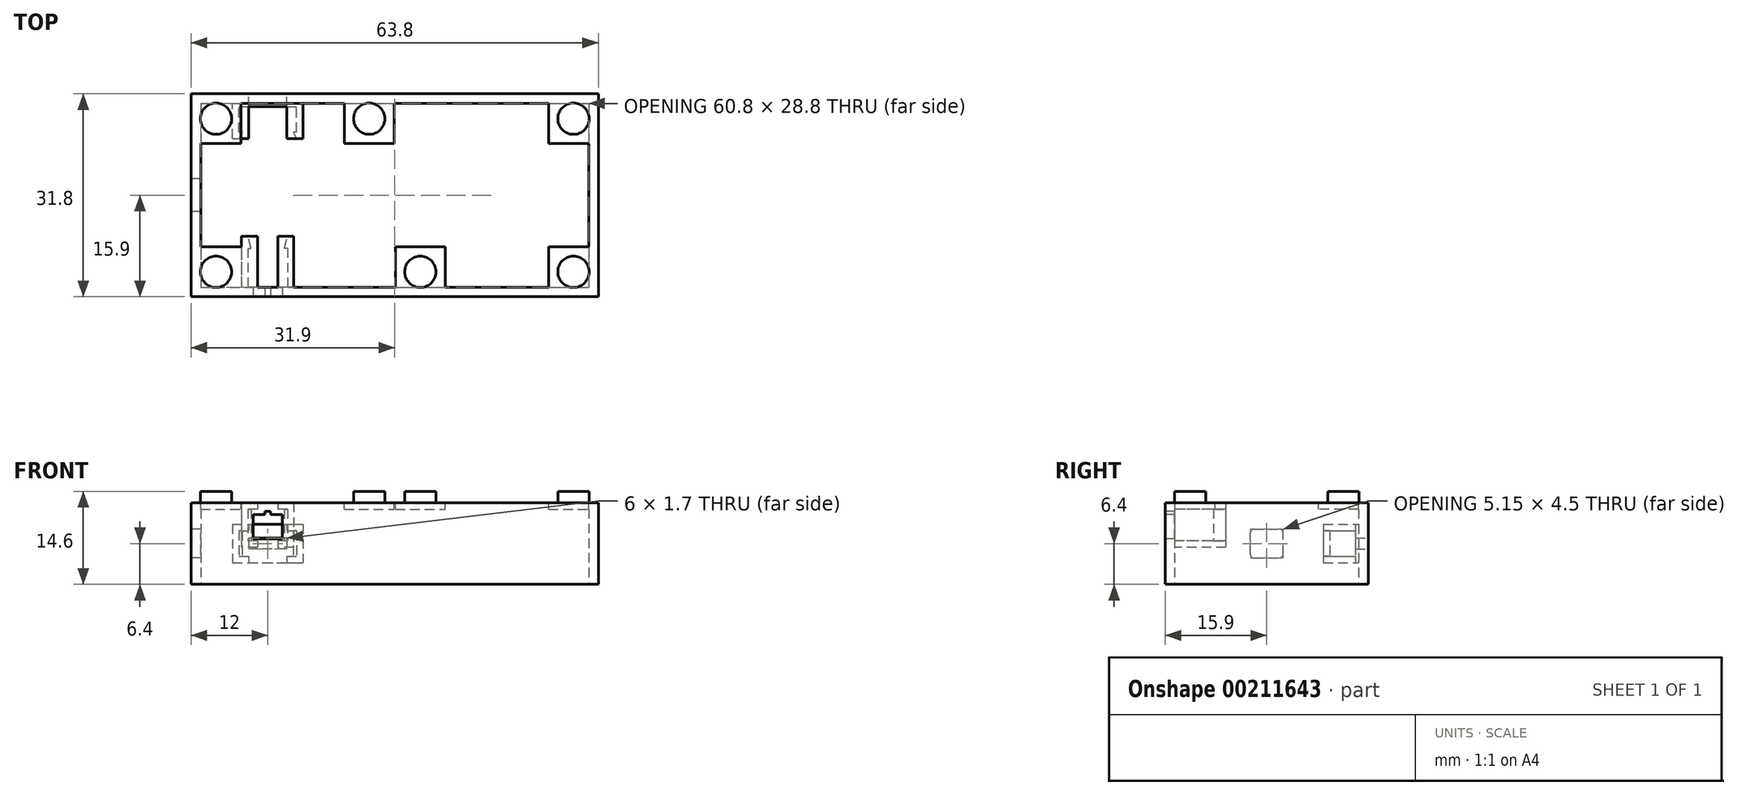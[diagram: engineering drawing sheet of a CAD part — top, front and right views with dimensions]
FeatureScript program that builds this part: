
annotation { "Feature Type Name" : "Feature", "Feature Type Description" : "" }
export const myFeature = defineFeature(function(context is Context, id is Id, definition is map)
    precondition{}
    {
        {
            var Q0;
            Q0=qCreatedBy(makeId("Top.planeOp"),FACE);
            var sketch = newSketch(context, id + "F0", { "sketchPlane" : qUnion([Q0])});
            skLineSegment(sketch, "E0.bottom", {"start": v(0, 31.8) * mm, "end": v(63.8, 31.8) * mm});
            skLineSegment(sketch, "E0.top", {"start": v(0, 0) * mm, "end": v(63.8, 0) * mm});
            skLineSegment(sketch, "E0.left", {"start": v(0, 31.8) * mm, "end": v(0, 0) * mm});
            skLineSegment(sketch, "E0.right", {"start": v(63.8, 31.8) * mm, "end": v(63.8, 0) * mm});
            skPoint(sketch, "E1", {"position": v(31.9, 31.8) * mm});
            skPoint(sketch, "E2", {"position": v(0, 15.9) * mm});
            skLineSegment(sketch, "E3.0", {"start": v(1.5, 30.3) * mm, "end": v(1.5, 1.5) * mm});
            skLineSegment(sketch, "E3.1", {"start": v(1.5, 30.3) * mm, "end": v(62.3, 30.3) * mm});
            skLineSegment(sketch, "E3.2", {"start": v(62.3, 30.3) * mm, "end": v(62.3, 1.5) * mm});
            skLineSegment(sketch, "E3.3", {"start": v(1.5, 1.5) * mm, "end": v(62.3, 1.5) * mm});
            skSolve(sketch);
        }
        {
            var Q0;
            Q0=qSketchRegion(id+"F0",true);
            extrude(context, id + "F1", {"entities" : qUnion([Q0]), "depth" : 12.8 * mm});
        }
        {
            var Q0;
            Q0=makeQuery(id+"F1.opExtrude","CAP_FACE",FACE,{"disambiguationData":[OSD([sQuery(id+"F0.wireOp",EDGE,"E0.bottom"),sQuery(id+"F0.wireOp",EDGE,"E0.top"),sQuery(id+"F0.wireOp",EDGE,"E0.left"),sQuery(id+"F0.wireOp",EDGE,"E0.right"),sQuery(id+"F0.wireOp",EDGE,"E3.0"),sQuery(id+"F0.wireOp",EDGE,"E3.1"),sQuery(id+"F0.wireOp",EDGE,"E3.2"),sQuery(id+"F0.wireOp",EDGE,"E3.3")])],"isStart":false});
            var sketch = newSketch(context, id + "F2", { "sketchPlane" : qUnion([Q0])});
            skLineSegment(sketch, "E4.bottom", {"start": v(0, 31.8) * mm, "end": v(7.8, 31.8) * mm});
            skLineSegment(sketch, "E4.top", {"start": v(0, 24) * mm, "end": v(7.8, 24) * mm});
            skLineSegment(sketch, "E4.left", {"start": v(0, 31.8) * mm, "end": v(0, 24) * mm});
            skLineSegment(sketch, "E4.right", {"start": v(7.8, 31.8) * mm, "end": v(7.8, 24) * mm});
            skLineSegment(sketch, "E5.bottom", {"start": v(0, 0) * mm, "end": v(7.8, 0) * mm});
            skLineSegment(sketch, "E5.top", {"start": v(0, 7.8) * mm, "end": v(7.8, 7.8) * mm});
            skLineSegment(sketch, "E5.left", {"start": v(0, 0) * mm, "end": v(0, 7.8) * mm});
            skLineSegment(sketch, "E5.right", {"start": v(7.8, 0) * mm, "end": v(7.8, 7.8) * mm});
            skLineSegment(sketch, "E6.bottom", {"start": v(63.8, 31.8) * mm, "end": v(56, 31.8) * mm});
            skLineSegment(sketch, "E6.top", {"start": v(63.8, 24) * mm, "end": v(56, 24) * mm});
            skLineSegment(sketch, "E6.left", {"start": v(63.8, 31.8) * mm, "end": v(63.8, 24) * mm});
            skLineSegment(sketch, "E6.right", {"start": v(56, 31.8) * mm, "end": v(56, 24) * mm});
            skLineSegment(sketch, "E7.bottom", {"start": v(63.8, 0) * mm, "end": v(56, 0) * mm});
            skLineSegment(sketch, "E7.top", {"start": v(63.8, 7.8) * mm, "end": v(56, 7.8) * mm});
            skLineSegment(sketch, "E7.left", {"start": v(63.8, 0) * mm, "end": v(63.8, 7.8) * mm});
            skLineSegment(sketch, "E7.right", {"start": v(56, 0) * mm, "end": v(56, 7.8) * mm});
            skPoint(sketch, "E8.centerSnap0", {"position": v(3.9, 24) * mm});
            skPoint(sketch, "E8.centerSnap1", {"position": v(0, 27.9) * mm});
            skPoint(sketch, "E9.centerSnap0", {"position": v(3.9, 0) * mm});
            skPoint(sketch, "E9.centerSnap1", {"position": v(0, 3.9) * mm});
            skPoint(sketch, "E10.centerSnap0", {"position": v(63.8, 27.9) * mm});
            skPoint(sketch, "E10.centerSnap1", {"position": v(59.9, 31.8) * mm});
            skPoint(sketch, "E11.centerSnap0", {"position": v(59.9, 0) * mm});
            skPoint(sketch, "E11.centerSnap1", {"position": v(63.8, 3.9) * mm});
            skLineSegment(sketch, "E12.bottom", {"start": v(24, 31.8) * mm, "end": v(31.8, 31.8) * mm});
            skLineSegment(sketch, "E12.top", {"start": v(24, 24) * mm, "end": v(31.8, 24) * mm});
            skLineSegment(sketch, "E12.left", {"start": v(24, 31.8) * mm, "end": v(24, 24) * mm});
            skLineSegment(sketch, "E12.right", {"start": v(31.8, 31.8) * mm, "end": v(31.8, 24) * mm});
            skLineSegment(sketch, "E13.bottom", {"start": v(39.8, 0) * mm, "end": v(32, 0) * mm});
            skLineSegment(sketch, "E13.top", {"start": v(39.8, 7.8) * mm, "end": v(32, 7.8) * mm});
            skLineSegment(sketch, "E13.left", {"start": v(39.8, 0) * mm, "end": v(39.8, 7.8) * mm});
            skLineSegment(sketch, "E13.right", {"start": v(32, 0) * mm, "end": v(32, 7.8) * mm});
            skPoint(sketch, "E14", {"position": v(27.9, 31.8) * mm});
            skPoint(sketch, "E15", {"position": v(35.9, 0) * mm});
            skSolve(sketch);
        }
        {
            var Q0;
            {var subQ0=sQuery(id+"F2.wireOp",EDGE,"E4.right");var subQ1=sQuery(id+"F2.wireOp",EDGE,"E4.top");var subQ2=makeQuery(id+"F2.imprint","INTERSECT",VERTEX,{"derivedFrom":[subQ1,subQ0]});Q0=makeQuery(id+"F2.imprint","IMPRINT",FACE,{"disambiguationData":[TD([[makeQuery(id+"F2.imprint","IMPRINT",EDGE,{"disambiguationData":[TD([[subQ2,1.0]])],"derivedFrom":subQ1}),1.0]])]});}
            var Q1;
            {var subQ0=sQuery(id+"F2.wireOp",EDGE,"E5.right");var subQ1=sQuery(id+"F2.wireOp",EDGE,"E5.top");var subQ2=makeQuery(id+"F2.imprint","INTERSECT",VERTEX,{"derivedFrom":[subQ1,subQ0]});Q1=makeQuery(id+"F2.imprint","IMPRINT",FACE,{"disambiguationData":[TD([[makeQuery(id+"F2.imprint","IMPRINT",EDGE,{"disambiguationData":[TD([[subQ2,1.0]])],"derivedFrom":subQ1}),-1.0]])]});}
            var Q2;
            {var subQ0=sQuery(id+"F2.wireOp",EDGE,"E7.right");var subQ1=sQuery(id+"F2.wireOp",EDGE,"E7.top");var subQ2=makeQuery(id+"F2.imprint","INTERSECT",VERTEX,{"derivedFrom":[subQ1,subQ0]});Q2=makeQuery(id+"F2.imprint","IMPRINT",FACE,{"disambiguationData":[TD([[makeQuery(id+"F2.imprint","IMPRINT",EDGE,{"disambiguationData":[TD([[subQ2,1.0]])],"derivedFrom":subQ1}),1.0]])]});}
            var Q3;
            {var subQ0=sQuery(id+"F2.wireOp",EDGE,"E6.right");var subQ1=sQuery(id+"F2.wireOp",EDGE,"E6.top");var subQ2=makeQuery(id+"F2.imprint","INTERSECT",VERTEX,{"derivedFrom":[subQ1,subQ0]});Q3=makeQuery(id+"F2.imprint","IMPRINT",FACE,{"disambiguationData":[TD([[makeQuery(id+"F2.imprint","IMPRINT",EDGE,{"disambiguationData":[TD([[subQ2,1.0]])],"derivedFrom":subQ1}),-1.0]])]});}
            var Q4;
            {var subQ0=sQuery(id+"F2.wireOp",EDGE,"E12.top");Q4=makeQuery(id+"F2.imprint","IMPRINT",FACE,{"disambiguationData":[TD([[makeQuery(id+"F2.imprint","IMPRINT",EDGE,{"derivedFrom":subQ0}),1.0]])]});}
            var Q5;
            {var subQ0=sQuery(id+"F2.wireOp",EDGE,"E13.top");Q5=makeQuery(id+"F2.imprint","IMPRINT",FACE,{"disambiguationData":[TD([[makeQuery(id+"F2.imprint","IMPRINT",EDGE,{"derivedFrom":subQ0}),1.0]])]});}
            extrude(context, id + "F3", {"entities" : qUnion([Q0, Q1, Q2, Q3, Q4, Q5]), "operationType" : NewBodyOperationType.ADD, "oppositeDirection" : true, "depth" : 1 * mm});
        }
        {
            var Q0;
            {var subQ0=sQuery(id+"F0.wireOp",EDGE,"E3.3");var subQ1=sQuery(id+"F0.wireOp",EDGE,"E3.2");var subQ2=sQuery(id+"F0.wireOp",EDGE,"E3.1");var subQ3=sQuery(id+"F0.wireOp",EDGE,"E3.0");Q0=makeQuery(id+"F3.boolean.opBoolean","MERGE",FACE,{"derivedFrom":[makeQuery(id+"F1.opExtrude","CAP_FACE",FACE,{"disambiguationData":[OSD([sQuery(id+"F0.wireOp",EDGE,"E0.bottom"),sQuery(id+"F0.wireOp",EDGE,"E0.top"),sQuery(id+"F0.wireOp",EDGE,"E0.left"),sQuery(id+"F0.wireOp",EDGE,"E0.right"),subQ3,subQ2,subQ1,subQ0])],"isStart":false}),makeQuery(id+"F3.opExtrude","CAP_FACE",FACE,{"disambiguationData":[OSD([subQ3,subQ2,sQuery(id+"F2.wireOp",EDGE,"E4.top"),sQuery(id+"F2.wireOp",EDGE,"E4.right")])],"isStart":true}),makeQuery(id+"F3.opExtrude","CAP_FACE",FACE,{"disambiguationData":[OSD([subQ3,subQ0,sQuery(id+"F2.wireOp",EDGE,"E5.top"),sQuery(id+"F2.wireOp",EDGE,"E5.right")])],"isStart":true}),makeQuery(id+"F3.opExtrude","CAP_FACE",FACE,{"disambiguationData":[OSD([subQ2,subQ1,sQuery(id+"F2.wireOp",EDGE,"E6.top"),sQuery(id+"F2.wireOp",EDGE,"E6.right")])],"isStart":true}),makeQuery(id+"F3.opExtrude","CAP_FACE",FACE,{"disambiguationData":[OSD([subQ1,subQ0,sQuery(id+"F2.wireOp",EDGE,"E7.top"),sQuery(id+"F2.wireOp",EDGE,"E7.right")])],"isStart":true})]});}
            var sketch = newSketch(context, id + "F4", { "sketchPlane" : qUnion([Q0])});
            skLineSegment(sketch, "E16.bottom", {"start": v(0, 31.8) * mm, "end": v(7.8, 31.8) * mm});
            skLineSegment(sketch, "E16.top", {"start": v(0, 24) * mm, "end": v(7.8, 24) * mm});
            skLineSegment(sketch, "E16.left", {"start": v(0, 31.8) * mm, "end": v(0, 24) * mm});
            skLineSegment(sketch, "E16.right", {"start": v(7.8, 31.8) * mm, "end": v(7.8, 24) * mm});
            skLineSegment(sketch, "E17.bottom", {"start": v(0, 0) * mm, "end": v(7.8, 0) * mm});
            skLineSegment(sketch, "E17.top", {"start": v(0, 7.8) * mm, "end": v(7.8, 7.8) * mm});
            skLineSegment(sketch, "E17.left", {"start": v(0, 0) * mm, "end": v(0, 7.8) * mm});
            skLineSegment(sketch, "E17.right", {"start": v(7.8, 0) * mm, "end": v(7.8, 7.8) * mm});
            skLineSegment(sketch, "E18.bottom", {"start": v(63.8, 31.8) * mm, "end": v(56, 31.8) * mm});
            skLineSegment(sketch, "E18.top", {"start": v(63.8, 24) * mm, "end": v(56, 24) * mm});
            skLineSegment(sketch, "E18.left", {"start": v(63.8, 31.8) * mm, "end": v(63.8, 24) * mm});
            skLineSegment(sketch, "E18.right", {"start": v(56, 31.8) * mm, "end": v(56, 24) * mm});
            skLineSegment(sketch, "E19.bottom", {"start": v(63.8, 0) * mm, "end": v(56, 0) * mm});
            skLineSegment(sketch, "E19.top", {"start": v(63.8, 7.8) * mm, "end": v(56, 7.8) * mm});
            skLineSegment(sketch, "E19.left", {"start": v(63.8, 0) * mm, "end": v(63.8, 7.8) * mm});
            skLineSegment(sketch, "E19.right", {"start": v(56, 0) * mm, "end": v(56, 7.8) * mm});
            skCircle(sketch, "E20", {"center": v(3.9, 27.9) * mm, "radius": 2.45 * mm});
            skPoint(sketch, "E20.centerSnap0", {"position": v(3.9, 31.8) * mm});
            skPoint(sketch, "E20.centerSnap1", {"position": v(0, 27.9) * mm});
            skCircle(sketch, "E21", {"center": v(3.9, 3.9) * mm, "radius": 2.45 * mm});
            skPoint(sketch, "E21.centerSnap0", {"position": v(3.9, 0) * mm});
            skPoint(sketch, "E21.centerSnap1", {"position": v(0, 3.9) * mm});
            skCircle(sketch, "E22", {"center": v(59.9, 27.9) * mm, "radius": 2.45 * mm});
            skPoint(sketch, "E22.centerSnap0", {"position": v(63.8, 27.9) * mm});
            skPoint(sketch, "E22.centerSnap1", {"position": v(59.9, 31.8) * mm});
            skCircle(sketch, "E23", {"center": v(59.9, 3.9) * mm, "radius": 2.45 * mm});
            skPoint(sketch, "E23.centerSnap0", {"position": v(59.9, 0) * mm});
            skPoint(sketch, "E23.centerSnap1", {"position": v(63.8, 3.9) * mm});
            skLineSegment(sketch, "E24.bottom", {"start": v(31.8, 24) * mm, "end": v(24, 24) * mm});
            skLineSegment(sketch, "E24.top", {"start": v(31.8, 31.8) * mm, "end": v(24, 31.8) * mm});
            skLineSegment(sketch, "E24.left", {"start": v(31.8, 24) * mm, "end": v(31.8, 31.8) * mm});
            skLineSegment(sketch, "E24.right", {"start": v(24, 24) * mm, "end": v(24, 31.8) * mm});
            skLineSegment(sketch, "E25.bottom", {"start": v(32, 7.8) * mm, "end": v(39.8, 7.8) * mm});
            skLineSegment(sketch, "E25.top", {"start": v(32, 0) * mm, "end": v(39.8, 0) * mm});
            skLineSegment(sketch, "E25.left", {"start": v(32, 7.8) * mm, "end": v(32, 0) * mm});
            skLineSegment(sketch, "E25.right", {"start": v(39.8, 7.8) * mm, "end": v(39.8, 0) * mm});
            skPoint(sketch, "E26", {"position": v(27.9, 31.8) * mm});
            skPoint(sketch, "E27", {"position": v(24, 27.9) * mm});
            skPoint(sketch, "E28", {"position": v(35.9, 7.8) * mm});
            skPoint(sketch, "E29", {"position": v(32, 3.9) * mm});
            skCircle(sketch, "E30", {"center": v(27.9, 27.9) * mm, "radius": 2.45 * mm});
            skCircle(sketch, "E31", {"center": v(35.9, 3.9) * mm, "radius": 2.45 * mm});
            skSolve(sketch);
        }
        {
            var Q0;
            Q0=makeQuery(id+"F4.imprint","IMPRINT",FACE,{"disambiguationData":[TD([[makeQuery(id+"F4.imprint","IMPRINT",EDGE,{"derivedFrom":sQuery(id+"F4.wireOp",EDGE,"E20")}),1.0]])]});
            var Q1;
            Q1=makeQuery(id+"F4.imprint","IMPRINT",FACE,{"disambiguationData":[TD([[makeQuery(id+"F4.imprint","IMPRINT",EDGE,{"derivedFrom":sQuery(id+"F4.wireOp",EDGE,"E22")}),1.0]])]});
            var Q2;
            Q2=makeQuery(id+"F4.imprint","IMPRINT",FACE,{"disambiguationData":[TD([[makeQuery(id+"F4.imprint","IMPRINT",EDGE,{"derivedFrom":sQuery(id+"F4.wireOp",EDGE,"E23")}),1.0]])]});
            var Q3;
            Q3=makeQuery(id+"F4.imprint","IMPRINT",FACE,{"disambiguationData":[TD([[makeQuery(id+"F4.imprint","IMPRINT",EDGE,{"derivedFrom":sQuery(id+"F4.wireOp",EDGE,"E21")}),1.0]])]});
            var Q4;
            Q4=makeQuery(id+"F4.imprint","IMPRINT",FACE,{"disambiguationData":[TD([[makeQuery(id+"F4.imprint","IMPRINT",EDGE,{"derivedFrom":sQuery(id+"F4.wireOp",EDGE,"E30")}),1.0]])]});
            var Q5;
            Q5=makeQuery(id+"F4.imprint","IMPRINT",FACE,{"disambiguationData":[TD([[makeQuery(id+"F4.imprint","IMPRINT",EDGE,{"derivedFrom":sQuery(id+"F4.wireOp",EDGE,"E31")}),1.0]])]});
            extrude(context, id + "F5", {"entities" : qUnion([Q0, Q1, Q2, Q3, Q4, Q5]), "operationType" : NewBodyOperationType.ADD, "depth" : 1.8 * mm});
        }
        {
            var Q0;
            Q0=makeQuery(id+"F1.opExtrude","SWEPT_FACE",FACE,{"disambiguationData":[OSD([sQuery(id+"F0.wireOp",EDGE,"E0.top")])]});
            var sketch = newSketch(context, id + "F6", { "sketchPlane" : qUnion([Q0])});
            skLineSegment(sketch, "E32.bottom", {"start": v(9.7, 10.95) * mm, "end": v(14.3, 10.95) * mm});
            skLineSegment(sketch, "E32.top", {"start": v(9.7, 7.15) * mm, "end": v(14.3, 7.15) * mm});
            skLineSegment(sketch, "E32.left", {"start": v(9.7, 10.95) * mm, "end": v(9.7, 7.15) * mm});
            skLineSegment(sketch, "E32.right", {"start": v(14.3, 10.95) * mm, "end": v(14.3, 7.15) * mm});
            skPoint(sketch, "E33", {"position": v(12, 12.8) * mm});
            skPoint(sketch, "E34", {"position": v(12, 10.95) * mm});
            skLineSegment(sketch, "E35.bottom", {"start": v(11.58, 11.45) * mm, "end": v(12.42, 11.45) * mm});
            skLineSegment(sketch, "E35.top", {"start": v(11.58, 10.95) * mm, "end": v(12.42, 10.95) * mm});
            skLineSegment(sketch, "E35.left", {"start": v(11.58, 11.45) * mm, "end": v(11.58, 10.95) * mm});
            skLineSegment(sketch, "E35.right", {"start": v(12.43, 11.45) * mm, "end": v(12.43, 10.95) * mm});
            skLineSegment(sketch, "E36", {"start": v(12, 11.8) * mm, "end": v(12, 6.8) * mm, "construction": true});
            skPoint(sketch, "E37", {"position": v(12, 9.3) * mm});
            skLineSegment(sketch, "E38", {"start": v(12, 11.45) * mm, "end": v(12, 7.15) * mm, "construction": true});
            skSolve(sketch);
        }
        {
            var Q0;
            Q0=makeQuery(id+"F6.imprint","IMPRINT",FACE,{"disambiguationData":[TD([[makeQuery(id+"F6.imprint","IMPRINT",EDGE,{"derivedFrom":sQuery(id+"F6.wireOp",EDGE,"E32.bottom")}),-1.0]])]});
            var Q1;
            Q1=makeQuery(id+"F6.imprint","IMPRINT",FACE,{"disambiguationData":[TD([[makeQuery(id+"F6.imprint","IMPRINT",EDGE,{"derivedFrom":sQuery(id+"F6.wireOp",EDGE,"b1744aed-7852-425b-a269-eb57eedebe04.bottom")}),-1.0]])]});
            var Q2;
            Q2=makeQuery(id+"F6.imprint","IMPRINT",FACE,{"disambiguationData":[TD([[makeQuery(id+"F6.imprint","IMPRINT",EDGE,{"derivedFrom":sQuery(id+"F6.wireOp",EDGE,"E35.bottom")}),-1.0]])]});
            extrude(context, id + "F7", {"entities" : qUnion([Q0, Q1, Q2]), "operationType" : NewBodyOperationType.REMOVE, "oppositeDirection" : true, "depth" : 25.4 * mm});
        }
        {
            var Q0;
            Q0=makeQuery(id+"F1.opExtrude","SWEPT_FACE",FACE,{"disambiguationData":[OSD([sQuery(id+"F0.wireOp",EDGE,"E3.3")])]});
            var sketch = newSketch(context, id + "F8", { "sketchPlane" : qUnion([Q0])});
            skLineSegment(sketch, "E39.0", {"start": v(-14.3, 7.15) * mm, "end": v(-14.3, 10.95) * mm});
            skLineSegment(sketch, "E40.0", {"start": v(-14.3, 10.95) * mm, "end": v(-12.43, 10.95) * mm});
            skLineSegment(sketch, "E41.0", {"start": v(-12.43, 10.95) * mm, "end": v(-12.43, 11.45) * mm});
            skPoint(sketch, "E42.0", {"position": v(-12, 11.45) * mm});
            skLineSegment(sketch, "E43.0", {"start": v(-12.43, 11.45) * mm, "end": v(-11.58, 11.45) * mm});
            skLineSegment(sketch, "E44.0", {"start": v(-11.58, 10.95) * mm, "end": v(-11.58, 11.45) * mm});
            skLineSegment(sketch, "E45.0", {"start": v(-11.58, 10.95) * mm, "end": v(-9.7, 10.95) * mm});
            skLineSegment(sketch, "E46.0", {"start": v(-9.7, 7.15) * mm, "end": v(-9.7, 10.95) * mm});
            skLineSegment(sketch, "E47.0", {"start": v(-14.3, 7.15) * mm, "end": v(-9.7, 7.15) * mm});
            skLineSegment(sketch, "E48.bottom", {"start": v(-15.1, 11.8) * mm, "end": v(-8.9, 11.8) * mm});
            skLineSegment(sketch, "E48.top", {"start": v(-15.1, 6.8) * mm, "end": v(-8.9, 6.8) * mm});
            skLineSegment(sketch, "E48.left", {"start": v(-15.1, 11.8) * mm, "end": v(-15.1, 6.8) * mm});
            skLineSegment(sketch, "E48.right", {"start": v(-8.9, 11.8) * mm, "end": v(-8.9, 6.8) * mm});
            skPoint(sketch, "E49", {"position": v(-12, 7.15) * mm});
            skPoint(sketch, "E50", {"position": v(-12, 6.8) * mm});
            skLineSegment(sketch, "E51", {"start": v(-12, 11.45) * mm, "end": v(-12, 7.15) * mm, "construction": true});
            skPoint(sketch, "E52", {"position": v(-12, 9.3) * mm});
            skPoint(sketch, "E53", {"position": v(-8.9, 9.3) * mm});
            skLineSegment(sketch, "E54.0", {"start": v(-16.1, 12.8) * mm, "end": v(-7.9, 12.8) * mm});
            skLineSegment(sketch, "E54.1", {"start": v(-16.1, 12.8) * mm, "end": v(-16.1, 5.8) * mm});
            skLineSegment(sketch, "E54.2", {"start": v(-16.1, 5.8) * mm, "end": v(-7.9, 5.8) * mm});
            skLineSegment(sketch, "E54.3", {"start": v(-7.9, 12.8) * mm, "end": v(-7.9, 5.8) * mm});
            skLineSegment(sketch, "E55.bottom", {"start": v(-16.1, 12.8) * mm, "end": v(-13.6, 12.8) * mm});
            skLineSegment(sketch, "E55.top", {"start": v(-16.1, 5.8) * mm, "end": v(-13.6, 5.8) * mm});
            skLineSegment(sketch, "E55.right", {"start": v(-13.6, 12.8) * mm, "end": v(-13.6, 5.8) * mm});
            skLineSegment(sketch, "E56.bottom", {"start": v(-7.9, 12.8) * mm, "end": v(-10.4, 12.8) * mm});
            skLineSegment(sketch, "E56.top", {"start": v(-7.9, 5.8) * mm, "end": v(-10.4, 5.8) * mm});
            skLineSegment(sketch, "E56.right", {"start": v(-10.4, 12.8) * mm, "end": v(-10.4, 5.8) * mm});
            skSolve(sketch);
        }
        {
            var Q0;
            {var subQ1=sQuery(id+"F8.wireOp",EDGE,"E48.left");Q0=makeQuery(id+"F8.imprint","IMPRINT",FACE,{"disambiguationData":[TD([[makeQuery(id+"F8.imprint","IMPRINT",EDGE,{"derivedFrom":subQ1}),-1.0]])]});}
            var Q1;
            {var subQ0=sQuery(id+"F8.wireOp",EDGE,"E48.right");Q1=makeQuery(id+"F8.imprint","IMPRINT",FACE,{"disambiguationData":[TD([[makeQuery(id+"F8.imprint","IMPRINT",EDGE,{"derivedFrom":subQ0}),1.0]])]});}
            extrude(context, id + "F9", {"entities" : qUnion([Q0, Q1]), "operationType" : NewBodyOperationType.ADD, "depth" : 8 * mm});
        }
        {
            var Q0;
            {var subQ0=sQuery(id+"F8.wireOp",EDGE,"E48.top");Q0=makeQuery(id+"F9.opExtrude","SWEPT_FACE",FACE,{"disambiguationData":[OSD([subQ0]),TDD([makeQuery(id+"F8.imprint","IMPRINT",EDGE,{"disambiguationData":[TD([[makeQuery(id+"F8.imprint","INTERSECT",VERTEX,{"derivedFrom":[subQ0,sQuery(id+"F8.wireOp",EDGE,"E48.left")]}),-1.0]])],"derivedFrom":subQ0})])]});}
            var sketch = newSketch(context, id + "F10", { "sketchPlane" : qUnion([Q0])});
            skLineSegment(sketch, "E57", {"start": v(15.1, 7.6) * mm, "end": v(14.6, 7.6) * mm});
            skLineSegment(sketch, "E58", {"start": v(14.6, 7.6) * mm, "end": v(15.1, 9.5) * mm});
            skLineSegment(sketch, "E59.0", {"start": v(8.9, 9.5) * mm, "end": v(8.9, 1.5) * mm});
            skLineSegment(sketch, "E60", {"start": v(8.9, 7.6) * mm, "end": v(9.4, 7.6) * mm});
            skLineSegment(sketch, "E61", {"start": v(9.4, 7.6) * mm, "end": v(8.9, 9.5) * mm});
            skSolve(sketch);
        }
        {
            var Q0;
            {var subQ0=sQuery(id+"F10.wireOp",EDGE,"E57");Q0=makeQuery(id+"F10.imprint","IMPRINT",FACE,{"disambiguationData":[TD([[makeQuery(id+"F10.imprint","IMPRINT",EDGE,{"derivedFrom":subQ0}),-1.0]])]});}
            var Q1;
            {var subQ2=sQuery(id+"F10.wireOp",EDGE,"E60");Q1=makeQuery(id+"F10.imprint","IMPRINT",FACE,{"disambiguationData":[TD([[makeQuery(id+"F10.imprint","IMPRINT",EDGE,{"derivedFrom":subQ2}),1.0]])]});}
            extrude(context, id + "F11", {"entities" : qUnion([Q0, Q1]), "operationType" : NewBodyOperationType.ADD, "endBound" : BoundingType.UP_TO_NEXT, "depth" : 25.4 * mm});
        }
        {
            var Q0;
            Q0=makeQuery(id+"F1.opExtrude","SWEPT_FACE",FACE,{"disambiguationData":[OSD([sQuery(id+"F0.wireOp",EDGE,"E3.3")])]});
            var sketch = newSketch(context, id + "F12", { "sketchPlane" : qUnion([Q0])});
            skLineSegment(sketch, "E62.bottom", {"start": v(-7.9, 12.8) * mm, "end": v(-4.9, 12.8) * mm});
            skLineSegment(sketch, "E62.top", {"start": v(-7.9, 11.8) * mm, "end": v(-4.9, 11.8) * mm});
            skLineSegment(sketch, "E62.left", {"start": v(-7.9, 12.8) * mm, "end": v(-7.9, 11.8) * mm});
            skLineSegment(sketch, "E62.right", {"start": v(-4.9, 12.8) * mm, "end": v(-4.9, 11.8) * mm});
            skSolve(sketch);
        }
        {
            var Q0;
            {var subQ2=sQuery(id+"F12.wireOp",EDGE,"E62.left");Q0=makeQuery(id+"F12.imprint","IMPRINT",FACE,{"disambiguationData":[TD([[makeQuery(id+"F12.imprint","IMPRINT",EDGE,{"derivedFrom":subQ2}),1.0]])]});}
            var Q1;
            Q1=makeQuery(id+"F3.opExtrude","SWEPT_FACE",FACE,{"disambiguationData":[OSD([sQuery(id+"F2.wireOp",EDGE,"E5.top")])]});
            extrude(context, id + "F13", {"entities" : qUnion([Q0]), "operationType" : NewBodyOperationType.ADD, "endBound" : BoundingType.UP_TO_SURFACE, "endBoundEntityFace" : qUnion([Q1]), "depth" : 25.4 * mm});
        }
        {
            var Q0;
            Q0=makeQuery(id+"F1.opExtrude","SWEPT_FACE",FACE,{"disambiguationData":[OSD([sQuery(id+"F0.wireOp",EDGE,"E0.bottom")])]});
            var sketch = newSketch(context, id + "F14", { "sketchPlane" : qUnion([Q0])});
            skLineSegment(sketch, "E63.bottom", {"start": v(-15, 7.25) * mm, "end": v(-9, 7.25) * mm});
            skLineSegment(sketch, "E63.top", {"start": v(-15, 5.55) * mm, "end": v(-9, 5.55) * mm});
            skLineSegment(sketch, "E63.left", {"start": v(-15, 7.25) * mm, "end": v(-15, 5.55) * mm});
            skLineSegment(sketch, "E63.right", {"start": v(-9, 7.25) * mm, "end": v(-9, 5.55) * mm});
            skPoint(sketch, "E64", {"position": v(0, 6.4) * mm});
            skPoint(sketch, "E65", {"position": v(-9, 6.4) * mm});
            skPoint(sketch, "E66", {"position": v(-12, 7.25) * mm});
            skSolve(sketch);
        }
        {
            var Q0;
            Q0=makeQuery(id+"F14.imprint","IMPRINT",FACE,{"disambiguationData":[TD([[makeQuery(id+"F14.imprint","IMPRINT",EDGE,{"derivedFrom":sQuery(id+"F14.wireOp",EDGE,"E63.bottom")}),-1.0]])]});
            extrude(context, id + "F15", {"entities" : qUnion([Q0]), "operationType" : NewBodyOperationType.REMOVE, "oppositeDirection" : true, "depth" : 2.54 * mm});
        }
        {
            var Q0;
            Q0=makeQuery(id+"F1.opExtrude","SWEPT_FACE",FACE,{"disambiguationData":[OSD([sQuery(id+"F0.wireOp",EDGE,"E3.1")])]});
            var sketch = newSketch(context, id + "F16", { "sketchPlane" : qUnion([Q0])});
            skLineSegment(sketch, "E67.bottom", {"start": v(6.5, 9.4) * mm, "end": v(17.5, 9.4) * mm});
            skLineSegment(sketch, "E67.top", {"start": v(6.5, 3.4) * mm, "end": v(17.5, 3.4) * mm});
            skLineSegment(sketch, "E67.left", {"start": v(6.5, 9.4) * mm, "end": v(6.5, 3.4) * mm});
            skLineSegment(sketch, "E67.right", {"start": v(17.5, 9.4) * mm, "end": v(17.5, 3.4) * mm});
            skPoint(sketch, "E68", {"position": v(12, 9.4) * mm});
            skPoint(sketch, "E69", {"position": v(12, 7.25) * mm});
            skPoint(sketch, "E70", {"position": v(15, 6.4) * mm});
            skPoint(sketch, "E71", {"position": v(17.5, 6.4) * mm});
            skSolve(sketch);
        }
        {
            var Q0;
            Q0=makeQuery(id+"F16.imprint","IMPRINT",FACE,{"disambiguationData":[TD([[makeQuery(id+"F16.imprint","IMPRINT",EDGE,{"derivedFrom":sQuery(id+"F16.wireOp",EDGE,"E67.bottom")}),-1.0]])]});
            extrude(context, id + "F17", {"entities" : qUnion([Q0]), "operationType" : NewBodyOperationType.ADD, "depth" : .5 * mm});
        }
        {
            var Q0;
            Q0=makeQuery(id+"F17.opExtrude","CAP_FACE",FACE,{"disambiguationData":[OSD([sQuery(id+"F0.wireOp",EDGE,"E3.1"),sQuery(id+"F14.wireOp",EDGE,"E63.bottom"),sQuery(id+"F14.wireOp",EDGE,"E63.top"),sQuery(id+"F14.wireOp",EDGE,"E63.left"),sQuery(id+"F14.wireOp",EDGE,"E63.right"),sQuery(id+"F16.wireOp",EDGE,"E67.bottom"),sQuery(id+"F16.wireOp",EDGE,"E67.top"),sQuery(id+"F16.wireOp",EDGE,"E67.left"),sQuery(id+"F16.wireOp",EDGE,"E67.right")])],"isStart":false});
            var sketch = newSketch(context, id + "F18", { "sketchPlane" : qUnion([Q0])});
            skLineSegment(sketch, "E72.0", {"start": v(6.5, 9.4) * mm, "end": v(6.5, 3.4) * mm});
            skLineSegment(sketch, "E72.1", {"start": v(6.5, 9.4) * mm, "end": v(17.5, 9.4) * mm});
            skLineSegment(sketch, "E72.2", {"start": v(17.5, 9.4) * mm, "end": v(17.5, 3.4) * mm});
            skLineSegment(sketch, "E72.3", {"start": v(6.5, 3.4) * mm, "end": v(17.5, 3.4) * mm});
            skLineSegment(sketch, "E73.bottom", {"start": v(7.5, 8.4) * mm, "end": v(16.5, 8.4) * mm});
            skLineSegment(sketch, "E73.top", {"start": v(7.5, 4.4) * mm, "end": v(16.5, 4.4) * mm});
            skLineSegment(sketch, "E73.left", {"start": v(7.5, 8.4) * mm, "end": v(7.5, 4.4) * mm});
            skLineSegment(sketch, "E73.right", {"start": v(16.5, 8.4) * mm, "end": v(16.5, 4.4) * mm});
            skPoint(sketch, "E74", {"position": v(12, 8.4) * mm});
            skPoint(sketch, "E75", {"position": v(12, 9.4) * mm});
            skPoint(sketch, "E76", {"position": v(16.5, 6.4) * mm});
            skPoint(sketch, "E77", {"position": v(17.5, 6.4) * mm});
            skLineSegment(sketch, "E78.bottom", {"start": v(17.5, 9.4) * mm, "end": v(15, 9.4) * mm});
            skLineSegment(sketch, "E78.top", {"start": v(17.5, 3.4) * mm, "end": v(15, 3.4) * mm});
            skLineSegment(sketch, "E78.right", {"start": v(15, 9.4) * mm, "end": v(15, 3.4) * mm});
            skLineSegment(sketch, "E79.bottom", {"start": v(6.5, 9.4) * mm, "end": v(9, 9.4) * mm});
            skLineSegment(sketch, "E79.top", {"start": v(6.5, 3.4) * mm, "end": v(9, 3.4) * mm});
            skLineSegment(sketch, "E79.right", {"start": v(9, 9.4) * mm, "end": v(9, 3.4) * mm});
            skSolve(sketch);
        }
        {
            var Q0;
            {var subQ1=sQuery(id+"F18.wireOp",EDGE,"E73.left");Q0=makeQuery(id+"F18.imprint","IMPRINT",FACE,{"disambiguationData":[TD([[makeQuery(id+"F18.imprint","IMPRINT",EDGE,{"derivedFrom":subQ1}),-1.0]])]});}
            var Q1;
            {var subQ1=sQuery(id+"F18.wireOp",EDGE,"E73.right");Q1=makeQuery(id+"F18.imprint","IMPRINT",FACE,{"disambiguationData":[TD([[makeQuery(id+"F18.imprint","IMPRINT",EDGE,{"derivedFrom":subQ1}),1.0]])]});}
            extrude(context, id + "F19", {"entities" : qUnion([Q0, Q1]), "operationType" : NewBodyOperationType.ADD, "depth" : 5 * mm});
        }
        {
            var Q0;
            {var subQ0=sQuery(id+"F18.wireOp",EDGE,"E73.top");Q0=makeQuery(id+"F19.opExtrude","SWEPT_FACE",FACE,{"disambiguationData":[OSD([subQ0]),TDD([makeQuery(id+"F18.imprint","IMPRINT",EDGE,{"disambiguationData":[TD([[makeQuery(id+"F18.imprint","INTERSECT",VERTEX,{"derivedFrom":[subQ0,sQuery(id+"F18.wireOp",EDGE,"E73.left")]}),-1.0]])],"derivedFrom":subQ0})])]});}
            var sketch = newSketch(context, id + "F20", { "sketchPlane" : qUnion([Q0])});
            skLineSegment(sketch, "E80.0", {"start": v(7.5, 24.8) * mm, "end": v(7.5, 29.8) * mm});
            skLineSegment(sketch, "E80.1", {"start": v(16.5, 24.8) * mm, "end": v(16.5, 29.8) * mm});
            skLineSegment(sketch, "E81", {"start": v(16.5, 25.8) * mm, "end": v(16, 25.8) * mm});
            skLineSegment(sketch, "E82", {"start": v(16, 25.8) * mm, "end": v(16.5, 24.8) * mm});
            skLineSegment(sketch, "E83", {"start": v(7.5, 25.8) * mm, "end": v(8, 25.8) * mm});
            skLineSegment(sketch, "E84", {"start": v(8, 25.8) * mm, "end": v(7.5, 24.8) * mm});
            skSolve(sketch);
        }
        {
            var Q0;
            {var subQ3=sQuery(id+"F20.wireOp",EDGE,"E83");Q0=makeQuery(id+"F20.imprint","IMPRINT",FACE,{"disambiguationData":[TD([[makeQuery(id+"F20.imprint","IMPRINT",EDGE,{"derivedFrom":subQ3}),-1.0]])]});}
            var Q1;
            {var subQ2=sQuery(id+"F20.wireOp",EDGE,"E81");Q1=makeQuery(id+"F20.imprint","IMPRINT",FACE,{"disambiguationData":[TD([[makeQuery(id+"F20.imprint","IMPRINT",EDGE,{"derivedFrom":subQ2}),1.0]])]});}
            extrude(context, id + "F21", {"entities" : qUnion([Q0, Q1]), "operationType" : NewBodyOperationType.ADD, "endBound" : BoundingType.UP_TO_NEXT, "depth" : 25.4 * mm});
        }
        {
            var Q0;
            Q0=makeQuery(id+"F1.opExtrude","SWEPT_FACE",FACE,{"disambiguationData":[OSD([sQuery(id+"F0.wireOp",EDGE,"E0.left")])]});
            var sketch = newSketch(context, id + "F22", { "sketchPlane" : qUnion([Q0])});
            skLineSegment(sketch, "E85.bottom", {"start": v(-17.9, 8.65) * mm, "end": v(-13.9, 8.65) * mm});
            skLineSegment(sketch, "E85.top", {"start": v(-17.9, 4.15) * mm, "end": v(-13.9, 4.15) * mm});
            skLineSegment(sketch, "E85.left", {"start": v(-18.48, 8.08) * mm, "end": v(-18.48, 4.72) * mm});
            skLineSegment(sketch, "E85.right", {"start": v(-13.32, 8.08) * mm, "end": v(-13.32, 4.72) * mm});
            skPoint(sketch, "E86", {"position": v(-15.9, 8.65) * mm});
            skPoint(sketch, "E87", {"position": v(-15.9, 12.8) * mm});
            skPoint(sketch, "E88", {"position": v(0, 6.4) * mm});
            skPoint(sketch, "E89", {"position": v(-13.32, 6.4) * mm});
            skPoint(sketch, "E90.visualSharp", {"position": v(-18.48, 8.65) * mm});
            skArc(sketch, "E90.filletArc", {"start": v(-17.9, 8.65) * mm, "mid": v(-18.3, 8.48) * mm, "end": v(-18.48, 8.08) * mm});
            skPoint(sketch, "E91.visualSharp", {"position": v(-13.32, 8.65) * mm});
            skArc(sketch, "E91.filletArc", {"start": v(-13.32, 8.08) * mm, "mid": v(-13.5, 8.48) * mm, "end": v(-13.9, 8.65) * mm});
            skPoint(sketch, "E92.visualSharp", {"position": v(-13.32, 4.15) * mm});
            skArc(sketch, "E92.filletArc", {"start": v(-13.9, 4.15) * mm, "mid": v(-13.5, 4.32) * mm, "end": v(-13.32, 4.72) * mm});
            skPoint(sketch, "E93.visualSharp", {"position": v(-18.48, 4.15) * mm});
            skArc(sketch, "E93.filletArc", {"start": v(-18.48, 4.72) * mm, "mid": v(-18.3, 4.32) * mm, "end": v(-17.9, 4.15) * mm});
            skSolve(sketch);
        }
        {
            var Q0;
            Q0=makeQuery(id+"F22.imprint","IMPRINT",FACE,{"disambiguationData":[TD([[makeQuery(id+"F22.imprint","IMPRINT",EDGE,{"derivedFrom":sQuery(id+"F22.wireOp",EDGE,"E85.bottom")}),-1.0]])]});
            extrude(context, id + "F23", {"entities" : qUnion([Q0]), "operationType" : NewBodyOperationType.REMOVE, "oppositeDirection" : true, "depth" : 25.4 * mm});
        }
    });
